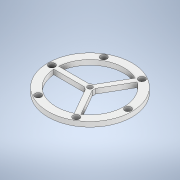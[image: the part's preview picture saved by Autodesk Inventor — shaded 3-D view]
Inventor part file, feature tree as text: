
AUTODESK INVENTOR PART (.ipt)
format: ipt  version: 2021 (Build 250183000, 183)  size: 153,600 bytes
history: native  units: mm
features: extrude x1, sketch x1
ambient origin geometry x8: Origin, YZ Plane, XZ Plane, XY Plane, X Axis, Y Axis, Z Axis, Center Point
bodies: Body1 (feature_tree)
feature tree (2):
  extrude  "Extrusion2"  Depth=6.0mm
  sketch  "Sketch1"  dims[d0=102.9mm d1=82.9mm d2=6.0mm d3=10.0mm d5=30.0mm d7=360.0deg d9=6.0mm d10=30.0mm d12=360.0deg d16=8.0mm d17=46.5mm d18=60.0mm d20=360.0deg d22=6.0mm d23=0.0mm]
